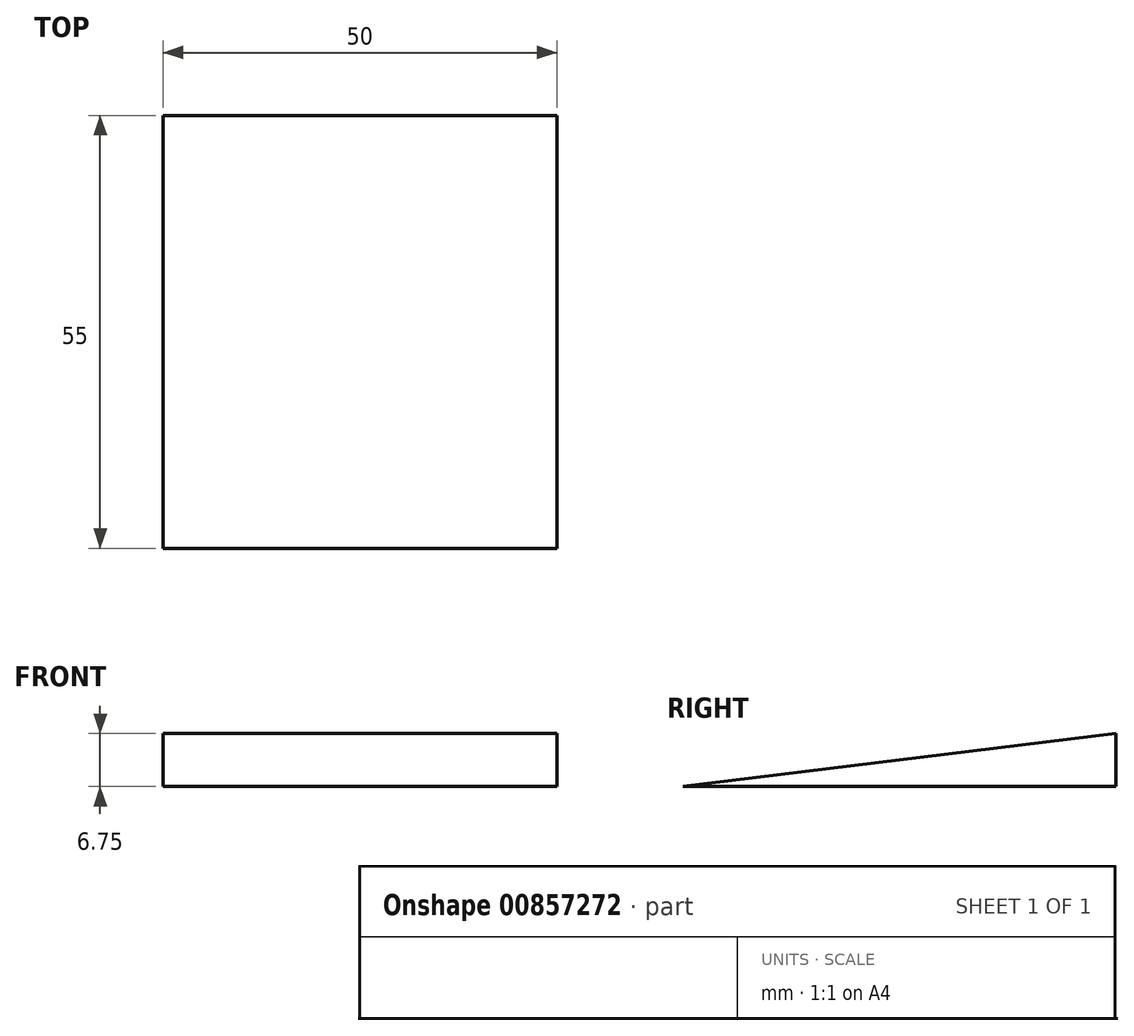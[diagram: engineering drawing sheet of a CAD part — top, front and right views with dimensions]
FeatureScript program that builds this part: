
annotation { "Feature Type Name" : "Feature", "Feature Type Description" : "" }
export const myFeature = defineFeature(function(context is Context, id is Id, definition is map)
    precondition{}
    {
        {
            var Q0;
            Q0=qCreatedBy(makeId("Top.planeOp"),FACE);
            var sketch = newSketch(context, id + "F0", { "sketchPlane" : qUnion([Q0])});
            skLineSegment(sketch, "E0.bottom", {"start": v(25, 27.5) * mm, "end": v(-25, 27.5) * mm});
            skLineSegment(sketch, "E0.top", {"start": v(25, -27.5) * mm, "end": v(-25, -27.5) * mm});
            skLineSegment(sketch, "E0.left", {"start": v(25, 27.5) * mm, "end": v(25, -27.5) * mm});
            skLineSegment(sketch, "E0.right", {"start": v(-25, 27.5) * mm, "end": v(-25, -27.5) * mm});
            skPoint(sketch, "E0.middle", {"position": v(0, 0) * mm});
            skSolve(sketch);
        }
        {
            var Q0;
            Q0=qCreatedBy(makeId("Top.planeOp"),FACE);
            var sketch = newSketch(context, id + "F1", { "sketchPlane" : qUnion([Q0])});
            skLineSegment(sketch, "E1", {"start": v(-25, -27.5) * mm, "end": v(25, -27.5) * mm});
            skSolve(sketch);
        }
        {
            var Q0;
            Q0=qBodyType(qCreatedBy(id+"F1",EDGE),BodyType.WIRE);
            cPlane(context, id + "F2", {"entities" : qUnion([Q0]), "cplaneType" : CPlaneType.LINE_ANGLE, "offset" : 25 * mm, "angle" : 97 * degree, "width" : 150 * mm, "height" : 150 * mm});
        }
        {
            var Q0;
            Q0=makeQuery(id+"F0.imprint","IMPRINT",FACE,{"disambiguationData":[TD([[makeQuery(id+"F0.imprint","IMPRINT",EDGE,{"derivedFrom":sQuery(id+"F0.wireOp",EDGE,"E0.bottom")}),1.0]])]});
            var Q1;
            Q1=qCreatedBy(id+"F2.planeOp",FACE);
            var Q2;
            Q2=qCreatedBy(id+"F2.planeOp",FACE);
            extrude(context, id + "F3", {"entities" : qUnion([Q0]), "endBound" : BoundingType.UP_TO_SURFACE, "depth" : 25 * mm, "endBoundEntityFace" : qUnion([Q1]), "offsetDistance" : 25 * mm});
        }
    });
